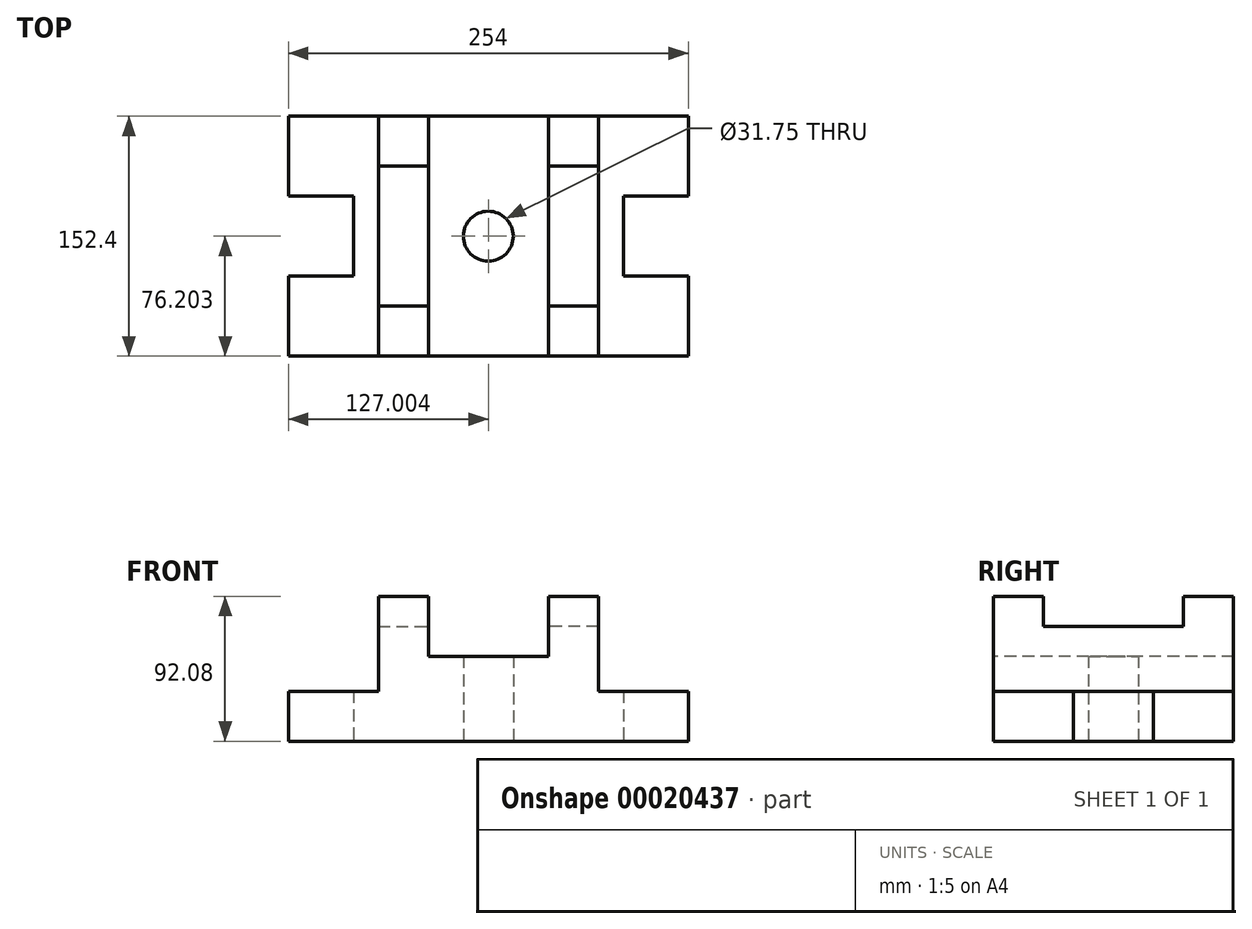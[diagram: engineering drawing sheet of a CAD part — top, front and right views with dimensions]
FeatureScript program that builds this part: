
annotation { "Feature Type Name" : "Feature", "Feature Type Description" : "" }
export const myFeature = defineFeature(function(context is Context, id is Id, definition is map)
    precondition{}
    {
        {
            var Q0;
            Q0=qCreatedBy(makeId("Top.planeOp"),FACE);
            var sketch = newSketch(context, id + "F0", { "sketchPlane" : qUnion([Q0])});
            skLineSegment(sketch, "E0.bottom", {"start": v(-70.06, -36.99) * mm, "end": v(56.94, -36.99) * mm});
            skLineSegment(sketch, "E0.top", {"start": v(-70.06, 115.41) * mm, "end": v(56.94, 115.41) * mm});
            skLineSegment(sketch, "E0.left", {"start": v(-70.06, -36.99) * mm, "end": v(-70.06, 115.41) * mm});
            skLineSegment(sketch, "E0.right", {"start": v(56.94, -36.99) * mm, "end": v(56.94, 13.81) * mm});
            skLineSegment(sketch, "E1.right", {"start": v(56.94, 115.41) * mm, "end": v(56.94, 64.61) * mm});
            skLineSegment(sketch, "E2", {"start": v(-0.2, 115.41) * mm, "end": v(-0.2, -36.99) * mm});
            skLineSegment(sketch, "E3", {"start": v(-31.96, 115.41) * mm, "end": v(-31.96, -36.99) * mm});
            skLineSegment(sketch, "E4", {"start": v(-31.96, 83.66) * mm, "end": v(0, 83.66) * mm});
            skLineSegment(sketch, "E5", {"start": v(0, 83.66) * mm, "end": v(-31.96, 83.66) * mm});
            skLineSegment(sketch, "E6", {"start": v(-31.96, -5.24) * mm, "end": v(0, -5.24) * mm});
            skLineSegment(sketch, "E7", {"start": v(0, -5.24) * mm, "end": v(-31.96, -5.24) * mm});
            skLineSegment(sketch, "E8", {"start": v(56.94, 13.81) * mm, "end": v(15.67, 13.81) * mm});
            skLineSegment(sketch, "E9", {"start": v(15.67, 13.81) * mm, "end": v(15.67, 64.61) * mm});
            skLineSegment(sketch, "E10", {"start": v(15.67, 64.61) * mm, "end": v(56.94, 64.61) * mm});
            skLineSegment(sketch, "E11.trimOffspring", {"start": v(56.94, 64.61) * mm, "end": v(56.94, 115.41) * mm});
            skLineSegment(sketch, "E12.trimOffspring", {"start": v(56.94, 13.81) * mm, "end": v(56.94, -36.99) * mm});
            skArc(sketch, "E13", {"start": v(-70.06, 23.34) * mm, "mid": v(-54.18, 39.21) * mm, "end": v(-70.06, 55.09) * mm});
            skSolve(sketch);
        }
        {
            var Q0;
            Q0=makeQuery(id+"F0.imprint","IMPRINT",FACE,{"disambiguationData":[TD([[makeQuery(id+"F0.imprint","IMPRINT",EDGE,{"derivedFrom":sQuery(id+"F0.wireOp",EDGE,"E8")}),1.0]])]});
            extrude(context, id + "F1", {"entities" : qUnion([Q0]), "depth" : 31.75 * mm});
        }
        {
            var Q0;
            {var subQ1=sQuery(id+"F0.wireOp",EDGE,"E2");var subQ5=sQuery(id+"F0.wireOp",EDGE,"E5");var subQ6=makeQuery(id+"F0.imprint","INTERSECT",VERTEX,{"derivedFrom":[subQ1,subQ5]});Q0=makeQuery(id+"F0.imprint","IMPRINT",FACE,{"disambiguationData":[TD([[makeQuery(id+"F0.imprint","IMPRINT",EDGE,{"disambiguationData":[TD([[subQ6,-1.0]])],"derivedFrom":subQ1}),-1.0]])]});}
            extrude(context, id + "F2", {"entities" : qUnion([Q0]), "operationType" : NewBodyOperationType.ADD, "depth" : 73.02 * mm});
        }
        {
            var Q0;
            {var subQ1=sQuery(id+"F0.wireOp",EDGE,"E2");var subQ5=sQuery(id+"F0.wireOp",EDGE,"E0.bottom");var subQ7=makeQuery(id+"F0.imprint","INTERSECT",VERTEX,{"derivedFrom":[subQ5,subQ1]});Q0=makeQuery(id+"F0.imprint","IMPRINT",FACE,{"disambiguationData":[TD([[makeQuery(id+"F0.imprint","IMPRINT",EDGE,{"disambiguationData":[TD([[subQ7,1.0]])],"derivedFrom":subQ5}),1.0]])]});}
            var Q1;
            {var subQ1=sQuery(id+"F0.wireOp",EDGE,"E2");var subQ5=sQuery(id+"F0.wireOp",EDGE,"E0.top");var subQ7=makeQuery(id+"F0.imprint","INTERSECT",VERTEX,{"derivedFrom":[subQ5,subQ1]});Q1=makeQuery(id+"F0.imprint","IMPRINT",FACE,{"disambiguationData":[TD([[makeQuery(id+"F0.imprint","IMPRINT",EDGE,{"disambiguationData":[TD([[subQ7,1.0]])],"derivedFrom":subQ5}),-1.0]])]});}
            extrude(context, id + "F3", {"entities" : qUnion([Q0, Q1]), "operationType" : NewBodyOperationType.ADD, "depth" : 92.07 * mm});
        }
        {
            var Q0;
            {var subQ5=sQuery(id+"F0.wireOp",EDGE,"E13");Q0=makeQuery(id+"F0.imprint","IMPRINT",FACE,{"disambiguationData":[TD([[makeQuery(id+"F0.imprint","IMPRINT",EDGE,{"derivedFrom":subQ5}),-1.0]])]});}
            extrude(context, id + "F4", {"entities" : qUnion([Q0]), "operationType" : NewBodyOperationType.ADD, "depth" : 53.97 * mm});
        }
        {
            var Q0;
            Q0=makeQuery(id+"F1.opExtrude","SWEPT_BODY",BODY,{"disambiguationData":[OSD([sQuery(id+"F0.wireOp",EDGE,"E0.bottom"),sQuery(id+"F0.wireOp",EDGE,"E0.top"),sQuery(id+"F0.wireOp",EDGE,"E2"),sQuery(id+"F0.wireOp",EDGE,"E8"),sQuery(id+"F0.wireOp",EDGE,"E9"),sQuery(id+"F0.wireOp",EDGE,"E10"),sQuery(id+"F0.wireOp",EDGE,"E11.trimOffspring"),sQuery(id+"F0.wireOp",EDGE,"E12.trimOffspring")])]});
            var Q1;
            {var subQ0=sQuery(id+"F0.wireOp",EDGE,"E0.left");Q1=makeQuery(id+"F4.opExtrude","SWEPT_FACE",FACE,{"disambiguationData":[OSD([subQ0]),TDD([makeQuery(id+"F0.imprint","IMPRINT",EDGE,{"disambiguationData":[TD([[makeQuery(id+"F0.imprint","INTERSECT",VERTEX,{"derivedFrom":[sQuery(id+"F0.wireOp",EDGE,"E0.top"),subQ0]}),1.0]])],"derivedFrom":subQ0})])]});}
            mirror(context, id + "F5", {"operationType" : NewBodyOperationType.ADD, "entities" : qUnion([Q0]), "mirrorPlane" : qUnion([Q1])});
        }
    });
